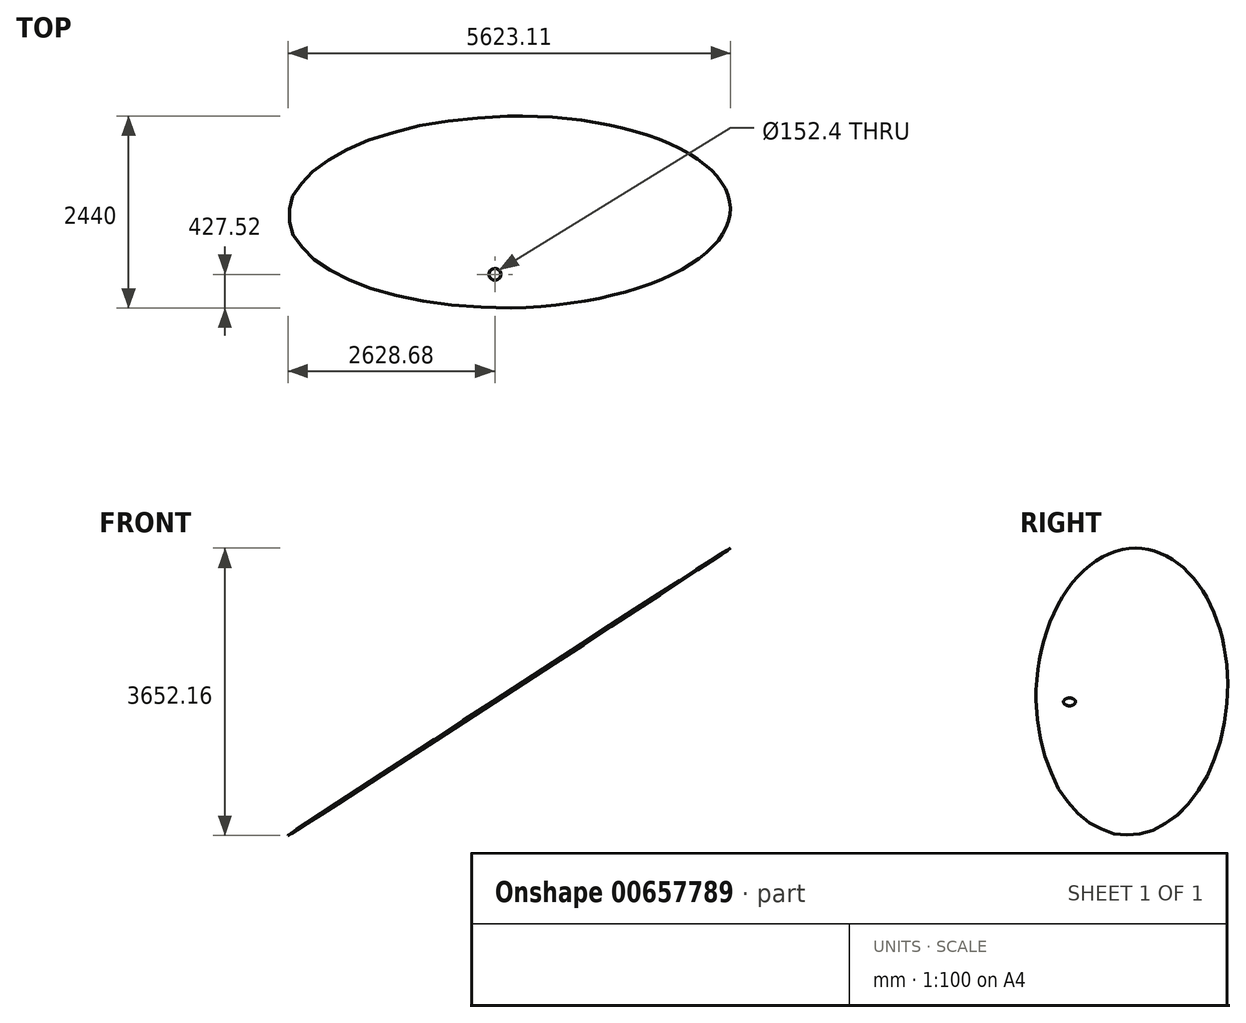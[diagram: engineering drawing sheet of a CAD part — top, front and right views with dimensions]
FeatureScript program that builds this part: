
annotation { "Feature Type Name" : "Feature", "Feature Type Description" : "" }
export const myFeature = defineFeature(function(context is Context, id is Id, definition is map)
    precondition{}
    {
        {
            assignVariable(context, id + "F0", {"name" : "Azimuth", "anyValue" : 179});
        }
        {
            assignVariable(context, id + "F1", {"name" : "Dip", "anyValue" : 33});
        }
        {
            assignVariable(context, id + "F2", {"name" : "Width", "anyValue" : 0.03});
        }
        {
            var Q0;
            Q0=qCreatedBy(makeId("Top.planeOp"),FACE);
            var sketch = newSketch(context, id + "F3", { "sketchPlane" : qUnion([Q0])});
            skEllipse(sketch, "E0", {"center": v(0, 0) * mm, "majorRadius": 1219.2 * mm, "minorRadius": 3352.8 * mm, "majorAxis": v(0, 1)});
            skLineSegment(sketch, "E1", {"start": v(0, 1219.2) * mm, "end": v(0, -1219.2) * mm, "construction": true});
            skLineSegment(sketch, "E2", {"start": v(-3093.72, 0) * mm, "end": v(3093.72, 0) * mm, "construction": true});
            skLineSegment(sketch, "E3.0", {"start": v(182.88, 1219.2) * mm, "end": v(182.88, -1219.2) * mm, "construction": true});
            skLineSegment(sketch, "E4.0", {"start": v(-3352.8, -792.48) * mm, "end": v(3352.8, -792.48) * mm, "construction": true});
            skSolve(sketch);
        }
        {
            var Q0;
            Q0=qCreatedBy(makeId("Top.planeOp"),FACE);
            var sketch = newSketch(context, id + "F4", { "sketchPlane" : qUnion([Q0])});
            skLineSegment(sketch, "E5", {"start": v(0, 0) * mm, "end": v(182.88, 0) * mm});
            skLineSegment(sketch, "E6", {"start": v(182.88, 0) * mm, "end": v(182.88, -792.48) * mm});
            skSolve(sketch);
        }
        {
            var Q0;
            Q0=qSketchRegion(id+"F3",true);
            extrude(context, id + "F5", {"entities" : qUnion([Q0]), "depth" : (getVariable(context, 'Width')) * mm});
        }
        {
            var Q0;
            Q0=qCreatedBy(makeId("Front.planeOp"),FACE);
            var sketch = newSketch(context, id + "F6", { "sketchPlane" : qUnion([Q0])});
            skLineSegment(sketch, "E7", {"start": v(0, 0) * mm, "end": v(0, -4572) * mm, "construction": true});
            skSolve(sketch);
        }
        {
            var Q0;
            Q0=makeQuery(id+"F5.opExtrude","SWEPT_BODY",BODY,{"disambiguationData":[OSD([sQuery(id+"F3.wireOp",EDGE,"E0"),sQuery(id+"F3.wireOp",EDGE,"TMMzbr5i-4nV4-ZnMr-aG6B-IGJ66UyS6uPJ")])]});
            var Q1;
            Q1=sQuery(id+"F3.wireOp",EDGE,"E1");
            transform(context, id + "F7", {"entities" : qUnion([Q0]), "transformType" : TransformType.ROTATION, "transformAxis" : qUnion([Q1]), "angle" : (getVariable(context, 'Dip')) * degree, "oppositeDirection" : true, "makeCopy" : false});
        }
        {
            var Q0;
            Q0=makeQuery(id+"F5.opExtrude","SWEPT_BODY",BODY,{"disambiguationData":[OSD([sQuery(id+"F3.wireOp",EDGE,"E0")])]});
            var Q1;
            Q1=sQuery(id+"F6.wireOp",EDGE,"E7");
            transform(context, id + "F8", {"entities" : qUnion([Q0]), "transformType" : TransformType.ROTATION, "transformAxis" : qUnion([Q1]), "angle" : (getVariable(context, 'Azimuth')) * degree, "makeCopy" : false});
        }
        {
            var Q0;
            Q0=makeQuery(id+"F5.opExtrude","SWEPT_BODY",BODY,{"disambiguationData":[OSD([sQuery(id+"F3.wireOp",EDGE,"E0"),sQuery(id+"F3.wireOp",EDGE,"TMMzbr5i-4nV4-ZnMr-aG6B-IGJ66UyS6uPJ")])]});
            var Q1;
            Q1=sQuery(id+"F4.wireOp",EDGE,"E5");
            transform(context, id + "F9", {"entities" : qUnion([Q0]), "transformType" : TransformType.TRANSLATION_ENTITY, "oppositeDirectionEntity" : false, "transformLine" : qUnion([Q1]), "makeCopy" : false});
        }
        {
            var Q0;
            Q0=makeQuery(id+"F5.opExtrude","SWEPT_BODY",BODY,{"disambiguationData":[OSD([sQuery(id+"F3.wireOp",EDGE,"E0"),sQuery(id+"F3.wireOp",EDGE,"TMMzbr5i-4nV4-ZnMr-aG6B-IGJ66UyS6uPJ")])]});
            var Q1;
            Q1=sQuery(id+"F4.wireOp",EDGE,"E6");
            transform(context, id + "F10", {"entities" : qUnion([Q0]), "transformType" : TransformType.TRANSLATION_ENTITY, "oppositeDirectionEntity" : true, "transformLine" : qUnion([Q1]), "makeCopy" : false});
        }
        {
            var Q0;
            Q0=qCreatedBy(makeId("Top.planeOp"),FACE);
            var sketch = newSketch(context, id + "F11", { "sketchPlane" : qUnion([Q0])});
            skCircle(sketch, "E8", {"center": v(0, 0) * mm, "radius": 76.2 * mm});
            skSolve(sketch);
        }
        {
            var Q0;
            Q0=makeQuery(id+"F5.opExtrude","SWEPT_BODY",BODY,{"disambiguationData":[OSD([sQuery(id+"F3.wireOp",EDGE,"E0")])]});
            var Q1;
            Q1=sQuery(id+"F6.wireOp",EDGE,"E7");
            transform(context, id + "F12", {"entities" : qUnion([Q0]), "transformType" : TransformType.TRANSLATION_3D, "dx" : 0 * mm, "dy" : 0 * mm, "dz" : -9875.52 * mm, "makeCopy" : false});
        }
        {
            var Q0;
            Q0=qSketchRegion(id+"F11",true);
            extrude(context, id + "F13", {"entities" : qUnion([Q0]), "operationType" : NewBodyOperationType.REMOVE, "endBound" : BoundingType.THROUGH_ALL, "oppositeDirection" : true, "depth" : 30.48 * mm, "hasSecondDirection" : true, "secondDirectionBound" : SecondDirectionBoundingType.THROUGH_ALL, "secondDirectionOppositeDirection" : false, "secondDirectionDepth" : 30.48 * mm});
        }
    });
